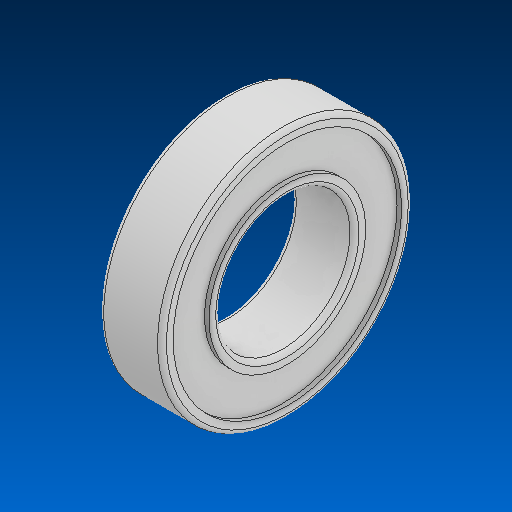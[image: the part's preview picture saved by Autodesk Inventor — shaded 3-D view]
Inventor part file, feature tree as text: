
AUTODESK INVENTOR PART (.ipt)
format: ipt  version: 2022.2 (Build 262287000, 287)  size: 177,664 bytes
history: native  units: in
note: dims shown in document units (in); Inventor stores cm internally (conversion verified against a paired STEP export)
features: fillet x1
ambient origin geometry x8: Origin, YZ Plane, XZ Plane, XY Plane, X Axis, Y Axis, Z Axis, Center Point
bodies: Solid1 (feature_tree)
feature tree (1):
  fillet  "Fillet1"  [1 undecoded]
note: 1 required parameter value undecoded (feature->parameter linkage not recoverable at this tier; creation-order binding heuristic only, values carry confidence <= 0.55)
